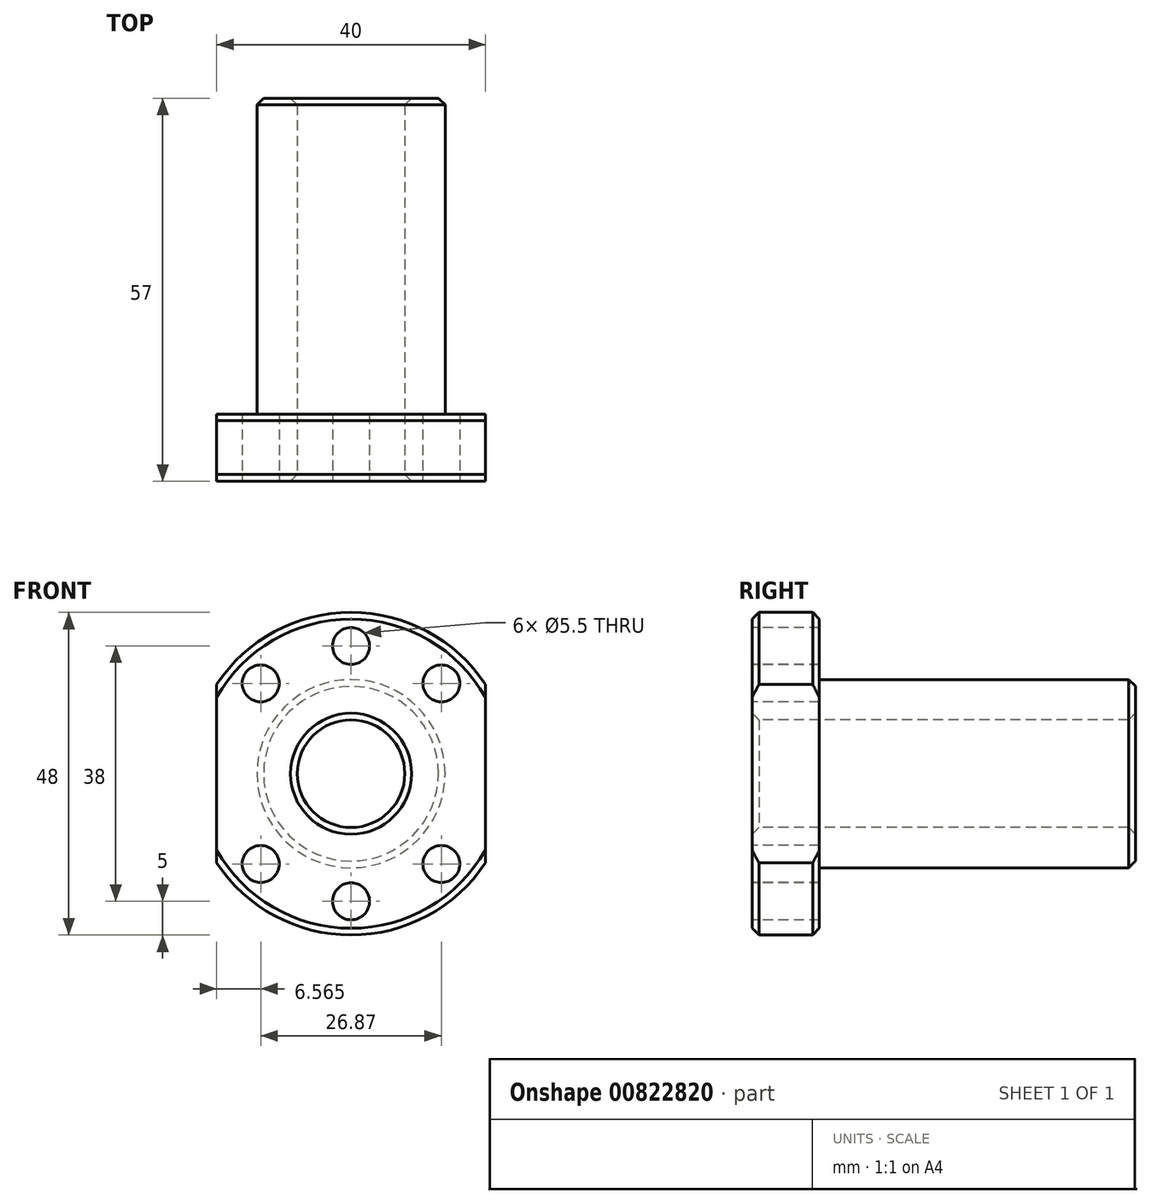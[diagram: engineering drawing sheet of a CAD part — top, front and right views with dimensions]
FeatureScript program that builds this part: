
annotation { "Feature Type Name" : "Feature", "Feature Type Description" : "" }
export const myFeature = defineFeature(function(context is Context, id is Id, definition is map)
    precondition{}
    {
        {
            var Q0;
            Q0=qCreatedBy(makeId("Right.planeOp"),FACE);
            var sketch = newSketch(context, id + "F0", { "sketchPlane" : qUnion([Q0])});
            skLineSegment(sketch, "E0", {"start": v(0, 24) * mm, "end": v(0, 8) * mm});
            skLineSegment(sketch, "E1", {"start": v(0, 8) * mm, "end": v(57, 8) * mm});
            skLineSegment(sketch, "E2", {"start": v(57, 8) * mm, "end": v(57, 14) * mm});
            skLineSegment(sketch, "E3", {"start": v(57, 14) * mm, "end": v(10, 14) * mm});
            skLineSegment(sketch, "E4", {"start": v(10, 14) * mm, "end": v(10, 24) * mm});
            skLineSegment(sketch, "E5", {"start": v(10, 24) * mm, "end": v(0, 24) * mm});
            skLineSegment(sketch, "E6", {"start": v(0, 0) * mm, "end": v(35.3, 0) * mm, "construction": true});
            skSolve(sketch);
        }
        {
            var Q0;
            Q0 = qSketchRegion(id + "F0", true);
            var Q1;
            Q1=sQuery(id+"F0.wireOp",EDGE,"E6");
            revolve(context, id + "F1", {"surfaceOperationType" : NewSurfaceOperationType.NEW, "entities" : qUnion([Q0]), "axis" : qUnion([Q1]), "revolveType" : RevolveType.FULL});
        }
        {
            var Q0;
            Q0=makeQuery(id+"F1.opRevolve","SWEPT_FACE",FACE,{"disambiguationData":[OSD([sQuery(id+"F0.wireOp",EDGE,"E0")])]});
            var sketch = newSketch(context, id + "F2", { "sketchPlane" : qUnion([Q0])});
            skLineSegment(sketch, "E7.bottom", {"start": v(-20, -63.13) * mm, "end": v(20, -63.13) * mm});
            skLineSegment(sketch, "E7.top", {"start": v(-20, 63.13) * mm, "end": v(20, 63.13) * mm});
            skLineSegment(sketch, "E7.left", {"start": v(-20, -63.13) * mm, "end": v(-20, 63.13) * mm});
            skLineSegment(sketch, "E7.right", {"start": v(20, -63.13) * mm, "end": v(20, 63.13) * mm});
            skPoint(sketch, "E7.middle", {"position": v(0, 0) * mm});
            skLineSegment(sketch, "E8.0", {"start": v(36.94, -80.06) * mm, "end": v(36.94, 80.06) * mm});
            skLineSegment(sketch, "E8.1", {"start": v(-36.94, -80.06) * mm, "end": v(36.94, -80.06) * mm});
            skLineSegment(sketch, "E8.2", {"start": v(-36.94, -80.06) * mm, "end": v(-36.94, 80.06) * mm});
            skLineSegment(sketch, "E8.3", {"start": v(-36.94, 80.06) * mm, "end": v(36.94, 80.06) * mm});
            skSolve(sketch);
        }
        {
            var Q0;
            Q0 = qSketchRegion(id + "F2", true);
            extrude(context, id + "F3", {"entities" : qUnion([Q0]), "operationType" : NewBodyOperationType.REMOVE, "oppositeDirection" : true, "depth" : 25 * mm, "offsetDistance" : 25 * mm});
        }
        {
            var Q0;
            Q0=makeQuery(id+"F1.opRevolve","SWEPT_FACE",FACE,{"disambiguationData":[OSD([sQuery(id+"F0.wireOp",EDGE,"E0")])]});
            var sketch = newSketch(context, id + "F4", { "sketchPlane" : qUnion([Q0])});
            skLineSegment(sketch, "E9.0.0", {"start": v(-20, 13.27) * mm, "end": v(-20, -13.27) * mm, "construction": true});
            skArc(sketch, "E9.0.1", {"start": v(-20, -13.27) * mm, "mid": v(0, -24) * mm, "end": v(20, -13.27) * mm, "construction": true});
            skLineSegment(sketch, "E9.0.2", {"start": v(20, -13.27) * mm, "end": v(20, 13.27) * mm, "construction": true});
            skArc(sketch, "E9.0.3", {"start": v(20, 13.27) * mm, "mid": v(0, 24) * mm, "end": v(-20, 13.27) * mm, "construction": true});
            skCircle(sketch, "E10.0", {"center": v(0, 0) * mm, "radius": 8 * mm, "construction": true});
            skLineSegment(sketch, "E11", {"start": v(0, -24) * mm, "end": v(0, 24) * mm, "construction": true});
            skLineSegment(sketch, "E12", {"start": v(-20, 0) * mm, "end": v(20, 0) * mm, "construction": true});
            skCircle(sketch, "E13", {"center": v(0, 0) * mm, "radius": 19 * mm, "construction": true});
            skCircle(sketch, "E14", {"center": v(0, 19) * mm, "radius": 2.75 * mm});
            skCircle(sketch, "E15.1.0", {"center": v(-13.44, 13.44) * mm, "radius": 2.75 * mm});
            skCircle(sketch, "E15.2.0", {"center": v(-19, 0) * mm, "radius": 2.75 * mm, "construction": true});
            skCircle(sketch, "E15.3.0", {"center": v(-13.44, -13.44) * mm, "radius": 2.75 * mm});
            skCircle(sketch, "E15.4.0", {"center": v(0, -19) * mm, "radius": 2.75 * mm});
            skCircle(sketch, "E15.5.0", {"center": v(13.44, -13.44) * mm, "radius": 2.75 * mm});
            skCircle(sketch, "E15.6.0", {"center": v(19, 0) * mm, "radius": 2.75 * mm, "construction": true});
            skCircle(sketch, "E15.7.0", {"center": v(13.44, 13.44) * mm, "radius": 2.75 * mm});
            skSolve(sketch);
        }
        {
            var Q0;
            Q0 = qSketchRegion(id + "F4", true);
            extrude(context, id + "F5", {"entities" : qUnion([Q0]), "operationType" : NewBodyOperationType.REMOVE, "oppositeDirection" : true, "depth" : 25 * mm, "offsetDistance" : 25 * mm});
        }
        {
            var Q0;
            Q0=makeQuery(id+"F1.opRevolve","SWEPT_FACE",FACE,{"disambiguationData":[OSD([sQuery(id+"F0.wireOp",EDGE,"E1")])]});
            var Q1;
            Q1=makeQuery(id+"F1.opRevolve","SWEPT_EDGE",EDGE,{"disambiguationData":[OSD([sQuery(id+"F0.wireOp",EDGE,"E2"),sQuery(id+"F0.wireOp",EDGE,"E3")])]});
            var Q2;
            Q2=makeQuery(id+"F3.boolean.opBoolean","SPLIT",EDGE,{"disambiguationData":[OD(1.0)],"derivedFrom":makeQuery(id+"F1.opRevolve","SWEPT_EDGE",EDGE,{"disambiguationData":[OSD([sQuery(id+"F0.wireOp",EDGE,"E0"),sQuery(id+"F0.wireOp",EDGE,"E5")])]})});
            var Q3;
            Q3=makeQuery(id+"F3.boolean.opBoolean","SPLIT",EDGE,{"disambiguationData":[OD(1.0)],"derivedFrom":makeQuery(id+"F1.opRevolve","SWEPT_EDGE",EDGE,{"disambiguationData":[OSD([sQuery(id+"F0.wireOp",EDGE,"E4"),sQuery(id+"F0.wireOp",EDGE,"E5")])]})});
            var Q4;
            Q4=makeQuery(id+"F3.boolean.opBoolean","SPLIT",EDGE,{"disambiguationData":[OD(0.0)],"derivedFrom":makeQuery(id+"F1.opRevolve","SWEPT_EDGE",EDGE,{"disambiguationData":[OSD([sQuery(id+"F0.wireOp",EDGE,"E4"),sQuery(id+"F0.wireOp",EDGE,"E5")])]})});
            var Q5;
            Q5=makeQuery(id+"F3.boolean.opBoolean","SPLIT",EDGE,{"disambiguationData":[OD(0.0)],"derivedFrom":makeQuery(id+"F1.opRevolve","SWEPT_EDGE",EDGE,{"disambiguationData":[OSD([sQuery(id+"F0.wireOp",EDGE,"E0"),sQuery(id+"F0.wireOp",EDGE,"E5")])]})});
            chamfer(context, id + "F6", {"entities" : qUnion([Q0, Q1, Q2, Q3, Q4, Q5]), "width" : 1 * mm, "tangentPropagation" : true});
        }
    });
